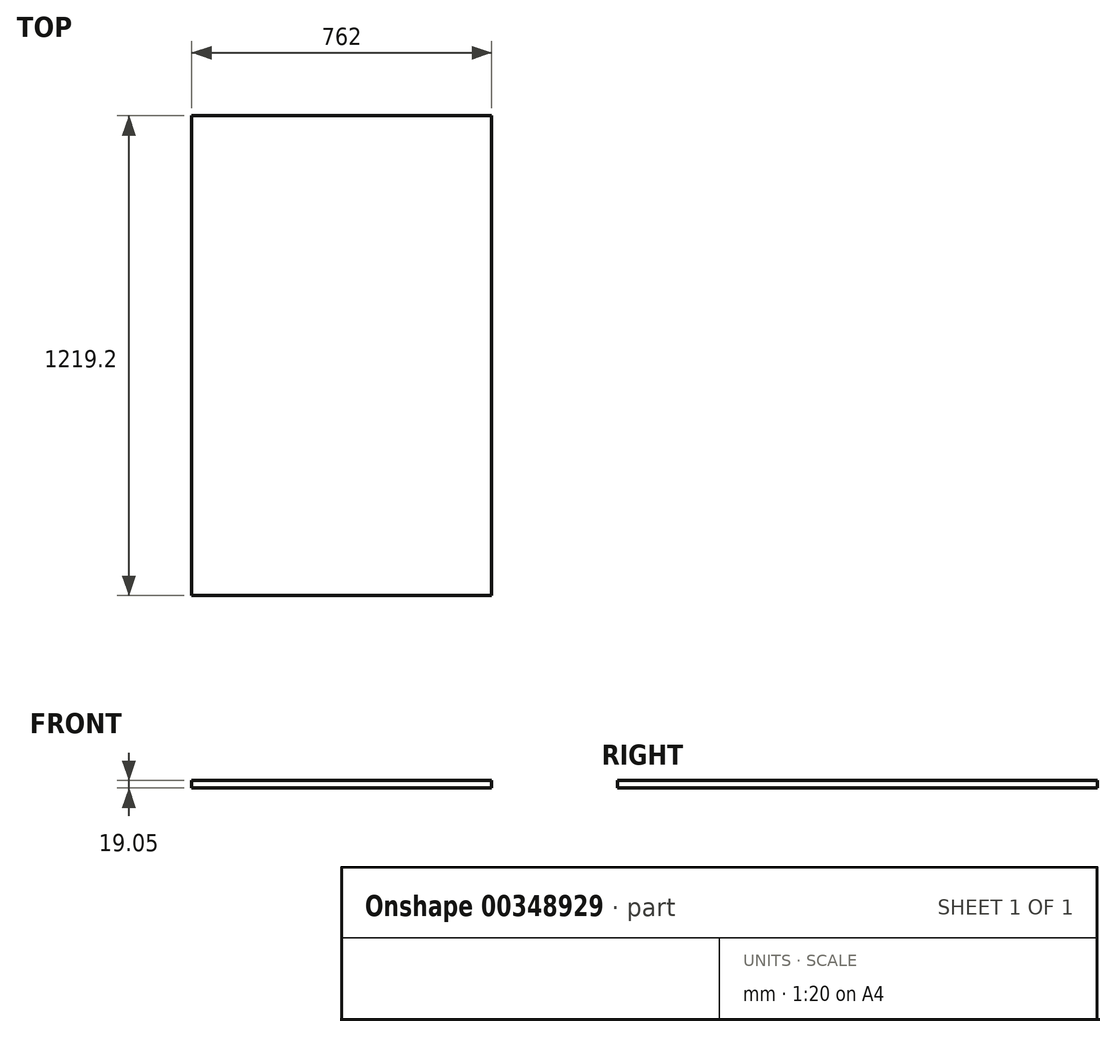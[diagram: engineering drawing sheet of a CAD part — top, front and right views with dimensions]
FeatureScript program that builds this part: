
annotation { "Feature Type Name" : "Feature", "Feature Type Description" : "" }
export const myFeature = defineFeature(function(context is Context, id is Id, definition is map)
    precondition{}
    {
        {
            var Q0;
            Q0=qCreatedBy(makeId("Front.planeOp"),FACE);
            var sketch = newSketch(context, id + "F0", { "sketchPlane" : qUnion([Q0])});
            skLineSegment(sketch, "E0.bottom", {"start": v(381, 0) * mm, "end": v(-381, 0) * mm});
            skLineSegment(sketch, "E0.top", {"start": v(381, 19.05) * mm, "end": v(-381, 19.05) * mm});
            skLineSegment(sketch, "E0.left", {"start": v(381, 0) * mm, "end": v(381, 19.05) * mm});
            skLineSegment(sketch, "E0.right", {"start": v(-381, 0) * mm, "end": v(-381, 19.05) * mm});
            skSolve(sketch);
        }
        {
            var Q0;
            Q0=makeQuery(id+"F0.imprint","IMPRINT",FACE,{"disambiguationData":[TD([[makeQuery(id+"F0.imprint","IMPRINT",EDGE,{"derivedFrom":sQuery(id+"F0.wireOp",EDGE,"E0.bottom")}),-1.0]])]});
            extrude(context, id + "F1", {"entities" : qUnion([Q0]), "oppositeDirection" : true, "depth" : 1219.2 * mm});
        }
    });
